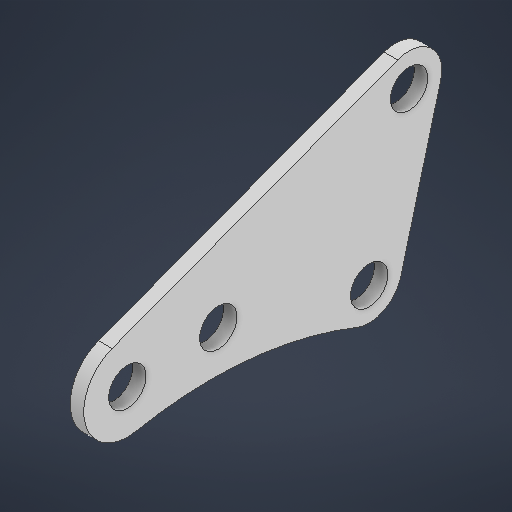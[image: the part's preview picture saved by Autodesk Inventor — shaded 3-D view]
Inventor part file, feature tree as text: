
AUTODESK INVENTOR PART (.ipt)
format: ipt  version: 2025.2 (Build 292293000, 293)  size: 204,288 bytes
history: native  units: in
note: dims shown in document units (in); Inventor stores cm internally (conversion verified against a paired STEP export)
features: extrude x1, sketch x1
ambient origin geometry x8: Origin, YZ Plane, XZ Plane, XY Plane, X Axis, Y Axis, Z Axis, Center Point
bodies: Solid1 (feature_tree)
feature tree (2):
  extrude  "Extrusion1"  Depth=0.0625in
  sketch  "Sketch1"  dims[d0=0.172in d1=0.3in d3=0.172in d4=0.4in d8=0.172in d11=0.172in d12=0.3in d13=0.3in d20=0.0625in d21=0.0in]
